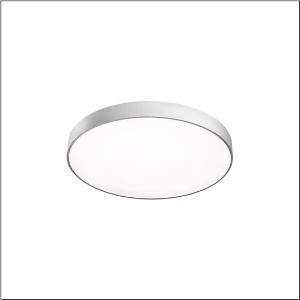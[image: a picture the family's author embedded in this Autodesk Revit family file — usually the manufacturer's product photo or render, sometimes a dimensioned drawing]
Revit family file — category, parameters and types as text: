
# Revit family: round_21_m_51mr36gm8421s
name_source: partatom
category: Lighting Fixtures
units: mm (PartAtom-declared; Revit-internal decimal feet)

## family parameters
Cut with Voids When Loaded = No
Host = Face
Light Source = No
Part Type = Normal
Room Calculation Point = No
Round Connector Dimension = Use Diameter
Shared = No

## types (1)
- --- (1 x LED, 8190 lm, 60.8 W, 4000K)
    Apparent Load = 61 VA
    CIE Flux Codes = 49 80 96 85 100
    Color Rendering = 80
    Color Temperature = 4000K
    Default Elevation = 1800 mm
    Description = Round 21 M, wall and ceiling luminaire, primary optical cover: cover, of PMMA, opal, light emission: direct/indirect distribution, primary light characteristic: symmetric, installation type: suspended mounting, surface-mounted, LED, rated luminous flux: 8.190lm, luminous efficacy: 135lm/W, light colour: 840, colour temperature: 4000K, with terminal, 3-pole, mains connection: 230V, AC, 50/60Hz, rated input power: 61W, housing, of aluminium, coated, silver, diameter: 600mm, height: 62mm, protection rating (complete): IP40, insulation class (complete): insulation class I (protective earthing), certification: CE, impact resistance: IK04, permissible operating ambient temperature: -10..+35°C, packaging unit: 1 piece
    Height = 87 mm
    Lamp = 1 x LED
    Lamp Light Flux = 8190 lm
    Lamp Power = 60.8 W
    Lamp count = 1
    Length = 600 mm
    Luminous efficacy = 135 lm/W
    Manufacturer = Siteco
    ModVariant = No
    Model = 51MR36GM8421S
    Mounting Place = Ceiling
    Mounting Type = Surface mounted
    Number of Poles = 1
    OnlyDefault = Yes
    Power Factor = 1
    Product Name = Round 21 M
    Product group = wall and ceiling luminaire
    ProductGroupID = 302
    Protection Class = Protection class I
    Protection Degree = IP 40
    RLX_Detail_Level = 1
    RLX_Emergency_Light_Flux = 0 lm
    RLX_Emergency_Type = 0
    RLX_Emergency_Type_DB = No
    RlxData = <blob elided: 17861 chars, md5=221091e2>
    Socket = socket
    Standby Power = 0 W
    System Light Flux = 8190 lm
    System Power = 61 W
    Type Comments = factory setting: luminous flux: 100 % | (ON | ON | ON | ON) | 700 mA
    Type Image = l_1258303.jpg
    URL = http://relux.com
    VarID = @adj_031919
    Voltage = 0 V
    Weight = 0.00 kg
    Width = 0 mm  [stored 0 ft]

note: [stored X ft] marks values corroborated as IEEE doubles in the binary element streams (Revit-internal decimal feet)

## geometry (parser evidence)
native form markers: Blend x4, Sweep x11
no freeform markers — native parametric forms only
